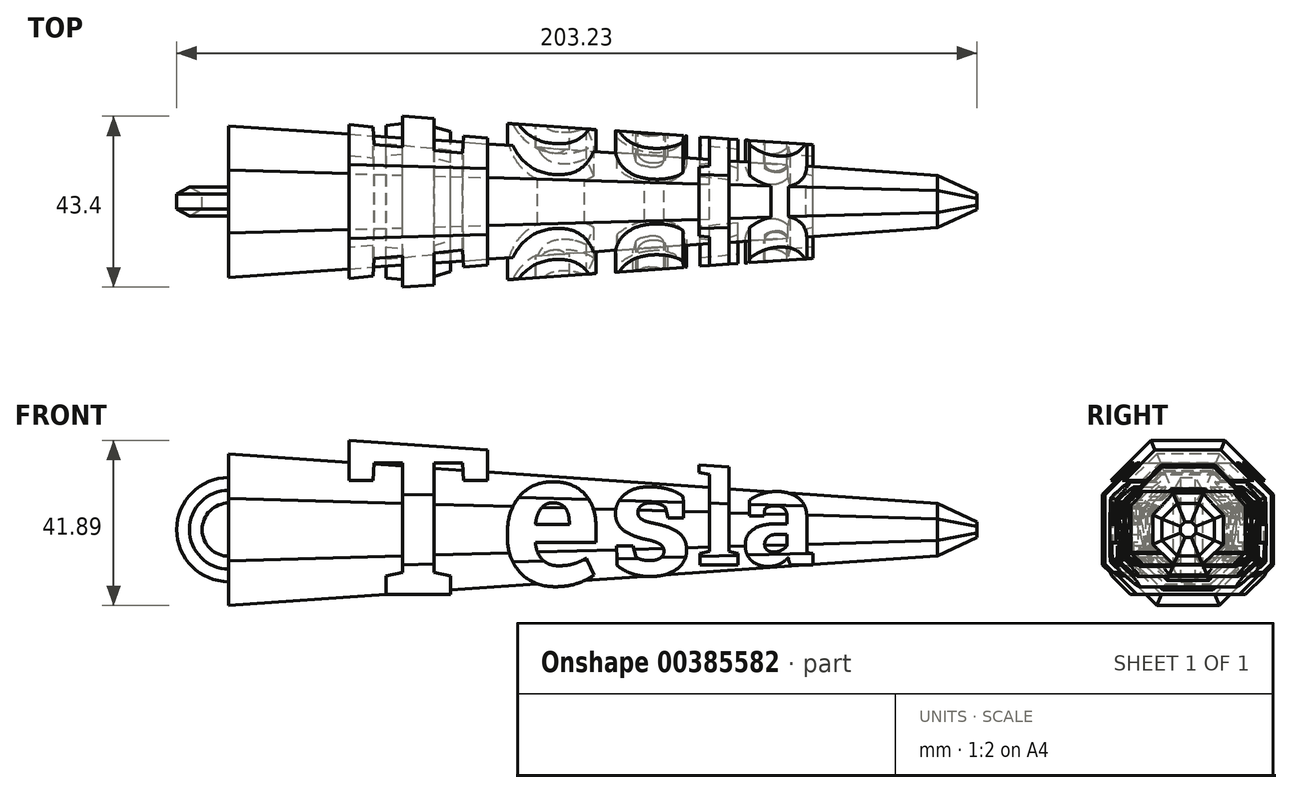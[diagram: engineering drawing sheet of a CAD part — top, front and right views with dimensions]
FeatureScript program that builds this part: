
annotation { "Feature Type Name" : "Feature", "Feature Type Description" : "" }
export const myFeature = defineFeature(function(context is Context, id is Id, definition is map)
    precondition{}
    {
        {
            assignVariable(context, id + "F0", {"name" : "hookPlane", "anyValue" : 90});
        }
        {
            assignVariable(context, id + "F1", {"name" : "halfLength", "anyValue" : 90});
        }
        {
            var Q0;
            Q0=qCreatedBy(makeId("Front.planeOp"),FACE);
            var sketch = newSketch(context, id + "F2", { "sketchPlane" : qUnion([Q0])});
            skText(sketch, "E0", { "text": "T", "fontName": "RobotoSlab-Bold.ttf"});
            skPoint(sketch, "E1", {"position": v(-20.83, 0) * mm});
            skText(sketch, "E2", { "text": "e", "fontName": "RobotoSlab-Bold.ttf"});
            skText(sketch, "E3", { "text": "s", "fontName": "RobotoSlab-Bold.ttf"});
            skText(sketch, "E4", { "text": "la", "fontName": "RobotoSlab-Bold.ttf"});
            skPoint(sketch, "E5", {"position": v(6.26, 0) * mm});
            skPoint(sketch, "E6", {"position": v(28.87, 0) * mm});
            skLineSegment(sketch, "E7", {"start": v(-60.53, -20) * mm, "end": v(-60.53, -51.65) * mm, "construction": true});
            skLineSegment(sketch, "E8", {"start": v(-60.53, -51.65) * mm, "end": v(60.53, -51.65) * mm, "construction": true});
            skLineSegment(sketch, "E9", {"start": v(60.53, -51.65) * mm, "end": v(60.53, -12.5) * mm, "construction": true});
            skPoint(sketch, "E10", {"position": v(0, -51.65) * mm});
            const initialGuessF2  = {"E0": [-0.06053, -0.02, 1, 0, 0.04], "E2": [-0.02083, -0.0175, 1, 0, 0.035], "E3": [0.00626, -0.015, 1, 0, 0.03], "E4": [0.02887, -0.0125, 1, 0, 0.025]};
            skSetInitialGuess(sketch, initialGuessF2);
            skSolve(sketch);
        }
        {
            var Q0;
            Q0=qSketchRegion(id+"F2",true);
            extrude(context, id + "F3", {"entities" : qUnion([Q0]), "depth" : 25 * mm, "hasSecondDirection" : true, "secondDirectionOppositeDirection" : true, "secondDirectionDepth" : 25 * mm});
        }
        {
            var Q0;
            Q0=qCreatedBy(makeId("Right.planeOp"),FACE);
            var sketch = newSketch(context, id + "F4", { "sketchPlane" : qUnion([Q0])});
            skCircle(sketch, "E11", {"center": v(0, -3.5) * mm, "radius": 12.5 * mm, "construction": true});
            skCircle(sketch, "E12.cCircle", {"center": v(0, -3.5) * mm, "radius": 12.95 * mm, "construction": true});
            skLineSegment(sketch, "E12.0", {"start": v(-5.36, 9.44) * mm, "end": v(5.36, 9.44) * mm});
            skLineSegment(sketch, "E12.1", {"start": v(5.36, 9.44) * mm, "end": v(12.95, 1.86) * mm});
            skLineSegment(sketch, "E12.2", {"start": v(12.95, 1.86) * mm, "end": v(12.95, -8.87) * mm});
            skLineSegment(sketch, "E12.3", {"start": v(12.95, -8.87) * mm, "end": v(5.36, -16.45) * mm});
            skLineSegment(sketch, "E12.4", {"start": v(5.36, -16.45) * mm, "end": v(-5.36, -16.45) * mm});
            skLineSegment(sketch, "E12.5", {"start": v(-5.36, -16.45) * mm, "end": v(-12.95, -8.87) * mm});
            skLineSegment(sketch, "E12.6", {"start": v(-12.95, -8.87) * mm, "end": v(-12.95, 1.86) * mm});
            skLineSegment(sketch, "E12.7", {"start": v(-12.95, 1.86) * mm, "end": v(-5.36, 9.44) * mm});
            skPoint(sketch, "E12.0.midPoint", {"position": v(0, 9.44) * mm});
            skLineSegment(sketch, "E13", {"start": v(0, 19.5) * mm, "end": v(0, 9.44) * mm, "construction": true});
            skSolve(sketch);
        }
        {
            var Q0;
            Q0=qSketchRegion(id+"F4",true);
            var Q1;
            Q1=makeQuery(id+"F3.opExtrude","SWEPT_FACE",FACE,{"disambiguationData":[OSD([sQuery(id+"F2.wireOp",EDGE,"E4.sketch_text.stroke-1")])]});
            extrude(context, id + "F5", {"entities" : qUnion([Q0]), "operationType" : NewBodyOperationType.ADD, "oppositeDirection" : true, "depth" : (getVariable(context, 'halfLength')) * mm, "hasDraft" : true, "draftAngle" : 4 * degree, "hasSecondDirection" : true, "secondDirectionOppositeDirection" : false, "secondDirectionBoundEntityFace" : qUnion([Q1]), "secondDirectionDepth" : (getVariable(context, 'halfLength')) * mm, "hasSecondDirectionDraft" : true, "secondDirectionDraftAngle" : 4 * degree, "secondDirectionDraftPullDirection" : true});
        }
        {
            var Q0;
            Q0=qCreatedBy(makeId("Right.planeOp"),FACE);
            var sketch = newSketch(context, id + "F6", { "sketchPlane" : qUnion([Q0])});
            skCircle(sketch, "E14.cCircle", {"center": v(0, -3.5) * mm, "radius": 18.5 * mm, "construction": true});
            skLineSegment(sketch, "E14.0", {"start": v(-7.66, 15) * mm, "end": v(7.66, 15) * mm});
            skLineSegment(sketch, "E14.1", {"start": v(7.66, 15) * mm, "end": v(18.5, 4.16) * mm});
            skLineSegment(sketch, "E14.2", {"start": v(18.5, 4.16) * mm, "end": v(18.5, -11.17) * mm});
            skLineSegment(sketch, "E14.3", {"start": v(18.5, -11.17) * mm, "end": v(7.66, -22) * mm});
            skLineSegment(sketch, "E14.4", {"start": v(7.66, -22) * mm, "end": v(-7.66, -22) * mm});
            skLineSegment(sketch, "E14.5", {"start": v(-7.66, -22) * mm, "end": v(-18.5, -11.17) * mm});
            skLineSegment(sketch, "E14.6", {"start": v(-18.5, -11.17) * mm, "end": v(-18.5, 4.16) * mm});
            skLineSegment(sketch, "E14.7", {"start": v(-18.5, 4.16) * mm, "end": v(-7.66, 15) * mm});
            skLineSegment(sketch, "E15.bottom", {"start": v(37.5, 34) * mm, "end": v(-37.5, 34) * mm});
            skLineSegment(sketch, "E15.top", {"start": v(37.5, -41) * mm, "end": v(-37.5, -41) * mm});
            skLineSegment(sketch, "E15.left", {"start": v(37.5, 34) * mm, "end": v(37.5, -41) * mm});
            skLineSegment(sketch, "E15.right", {"start": v(-37.5, 34) * mm, "end": v(-37.5, -41) * mm});
            skLineSegment(sketch, "E16", {"start": v(0, 19.5) * mm, "end": v(0, -8.52) * mm, "construction": true});
            skSolve(sketch);
        }
        {
            var Q0;
            Q0=makeQuery(id+"F6.imprint","IMPRINT",FACE,{"disambiguationData":[TD([[makeQuery(id+"F6.imprint","IMPRINT",EDGE,{"derivedFrom":sQuery(id+"F6.wireOp",EDGE,"E14.0")}),1.0]])]});
            extrude(context, id + "F7", {"entities" : qUnion([Q0]), "operationType" : NewBodyOperationType.REMOVE, "endBound" : BoundingType.THROUGH_ALL, "depth" : 25 * mm, "hasDraft" : true, "draftAngle" : 4 * degree, "hasSecondDirection" : true, "secondDirectionBound" : SecondDirectionBoundingType.THROUGH_ALL, "secondDirectionOppositeDirection" : true, "secondDirectionDepth" : 25 * mm, "hasSecondDirectionDraft" : true, "secondDirectionDraftAngle" : 4 * degree, "secondDirectionDraftPullDirection" : true});
        }
        {
            var Q0;
            {var subQ0=sQuery(id+"F4.wireOp",EDGE,"E12.3");var subQ1=sQuery(id+"F4.wireOp",EDGE,"E12.2");var subQ2=sQuery(id+"F4.wireOp",EDGE,"E12.4");var subQ3=sQuery(id+"F4.wireOp",EDGE,"E12.5");var subQ4=sQuery(id+"F4.wireOp",EDGE,"E12.6");Q0=makeQuery(id+"F5.boolean.opBoolean","SPLIT",FACE,{"disambiguationData":[TD([makeQuery(id+"F3.opExtrude","SWEPT_FACE",FACE,{"disambiguationData":[OSD([sQuery(id+"F2.wireOp",EDGE,"E4.sketch_text.stroke-0")])]})])],"derivedFrom":makeQuery(id+"F5.opExtrude","CAP_FACE",FACE,{"disambiguationData":[OSD([sQuery(id+"F4.wireOp",EDGE,"E12.0"),sQuery(id+"F4.wireOp",EDGE,"E12.1"),subQ1,subQ0,subQ2,subQ3,subQ4,sQuery(id+"F4.wireOp",EDGE,"E12.7")])],"isStart":true})});}
            var sketch = newSketch(context, id + "F8", { "sketchPlane" : qUnion([Q0])});
            skCircle(sketch, "E17.cCircle", {"center": v(0, -3.5) * mm, "radius": 6.65 * mm, "construction": true});
            skLineSegment(sketch, "E17.0", {"start": v(-2.76, 3.15) * mm, "end": v(2.76, 3.15) * mm});
            skLineSegment(sketch, "E17.1", {"start": v(2.76, 3.15) * mm, "end": v(6.65, -0.75) * mm});
            skLineSegment(sketch, "E17.2", {"start": v(6.65, -0.75) * mm, "end": v(6.65, -6.26) * mm});
            skLineSegment(sketch, "E17.3", {"start": v(6.65, -6.26) * mm, "end": v(2.76, -10.16) * mm});
            skLineSegment(sketch, "E17.4", {"start": v(2.76, -10.16) * mm, "end": v(-2.76, -10.16) * mm});
            skLineSegment(sketch, "E17.5", {"start": v(-2.76, -10.16) * mm, "end": v(-6.65, -6.26) * mm});
            skLineSegment(sketch, "E17.6", {"start": v(-6.65, -6.26) * mm, "end": v(-6.65, -0.75) * mm});
            skLineSegment(sketch, "E17.7", {"start": v(-6.65, -0.75) * mm, "end": v(-2.76, 3.15) * mm});
            skPoint(sketch, "E17.0.midPoint", {"position": v(0, 3.15) * mm});
            skLineSegment(sketch, "E18", {"start": v(0, 19.59) * mm, "end": v(0, -20.57) * mm, "construction": true});
            skSolve(sketch);
        }
        {
            var Q0;
            Q0=qSketchRegion(id+"F8",true);
            extrude(context, id + "F9", {"entities" : qUnion([Q0]), "operationType" : NewBodyOperationType.ADD, "depth" : 10 * mm, "hasDraft" : true, "draftAngle" : 25 * degree, "draftPullDirection" : true});
        }
        {
            var Q0;
            Q0=qCreatedBy(makeId("Right.planeOp"),FACE);
            cPlane(context, id + "F10", {"entities" : qUnion([Q0]), "cplaneType" : CPlaneType.OFFSET, "offset" : (getVariable(context, 'hookPlane')) * mm, "oppositeDirection" : true, "width" : 150 * mm, "height" : 150 * mm});
        }
        {
            var Q0;
            Q0=qCreatedBy(makeId("Front.planeOp"),FACE);
            var sketch = newSketch(context, id + "F11", { "sketchPlane" : qUnion([Q0])});
            skArc(sketch, "E19", {"start": v(-83.39, 4) * mm, "mid": v(-100, -3.5) * mm, "end": v(-83.39, -11) * mm});
            skLineSegment(sketch, "E20", {"start": v(-83.39, 4) * mm, "end": v(-83.39, -11) * mm, "construction": true});
            skPoint(sketch, "E21", {"position": v(-83.39, -3.5) * mm});
            skLineSegment(sketch, "E22", {"start": v(-90, 15.74) * mm, "end": v(-90, -22.74) * mm, "construction": true});
            skSolve(sketch);
        }
        {
            var Q0;
            Q0=qCreatedBy(id+"F10.planeOp",FACE);
            var sketch = newSketch(context, id + "F12", { "sketchPlane" : qUnion([Q0])});
            skCircle(sketch, "E23.cCircle", {"center": v(0, 6.5) * mm, "radius": 3.23 * mm, "construction": true});
            skLineSegment(sketch, "E23.0", {"start": v(1.87, 3.26) * mm, "end": v(-1.87, 3.26) * mm});
            skLineSegment(sketch, "E23.1", {"start": v(-1.87, 3.26) * mm, "end": v(-3.73, 6.5) * mm});
            skLineSegment(sketch, "E23.2", {"start": v(-3.73, 6.5) * mm, "end": v(-1.87, 9.73) * mm});
            skLineSegment(sketch, "E23.3", {"start": v(-1.87, 9.73) * mm, "end": v(1.87, 9.73) * mm});
            skLineSegment(sketch, "E23.4", {"start": v(1.87, 9.73) * mm, "end": v(3.73, 6.5) * mm});
            skLineSegment(sketch, "E23.5", {"start": v(3.73, 6.5) * mm, "end": v(1.87, 3.26) * mm});
            skPoint(sketch, "E23.0.midPoint", {"position": v(0, 3.26) * mm});
            skSolve(sketch);
        }
        {
            var Q0;
            Q0=qSketchRegion(id+"F12",true);
            var Q1;
            Q1=qConstructionFilter(qBodyType(qCreatedBy(id+"F11",EDGE),BodyType.WIRE),ConstructionObject.NO);
            sweep(context, id + "F13", {"operationType" : NewBodyOperationType.ADD, "profiles" : qUnion([Q0]), "path" : qUnion([Q1])});
        }
    });
